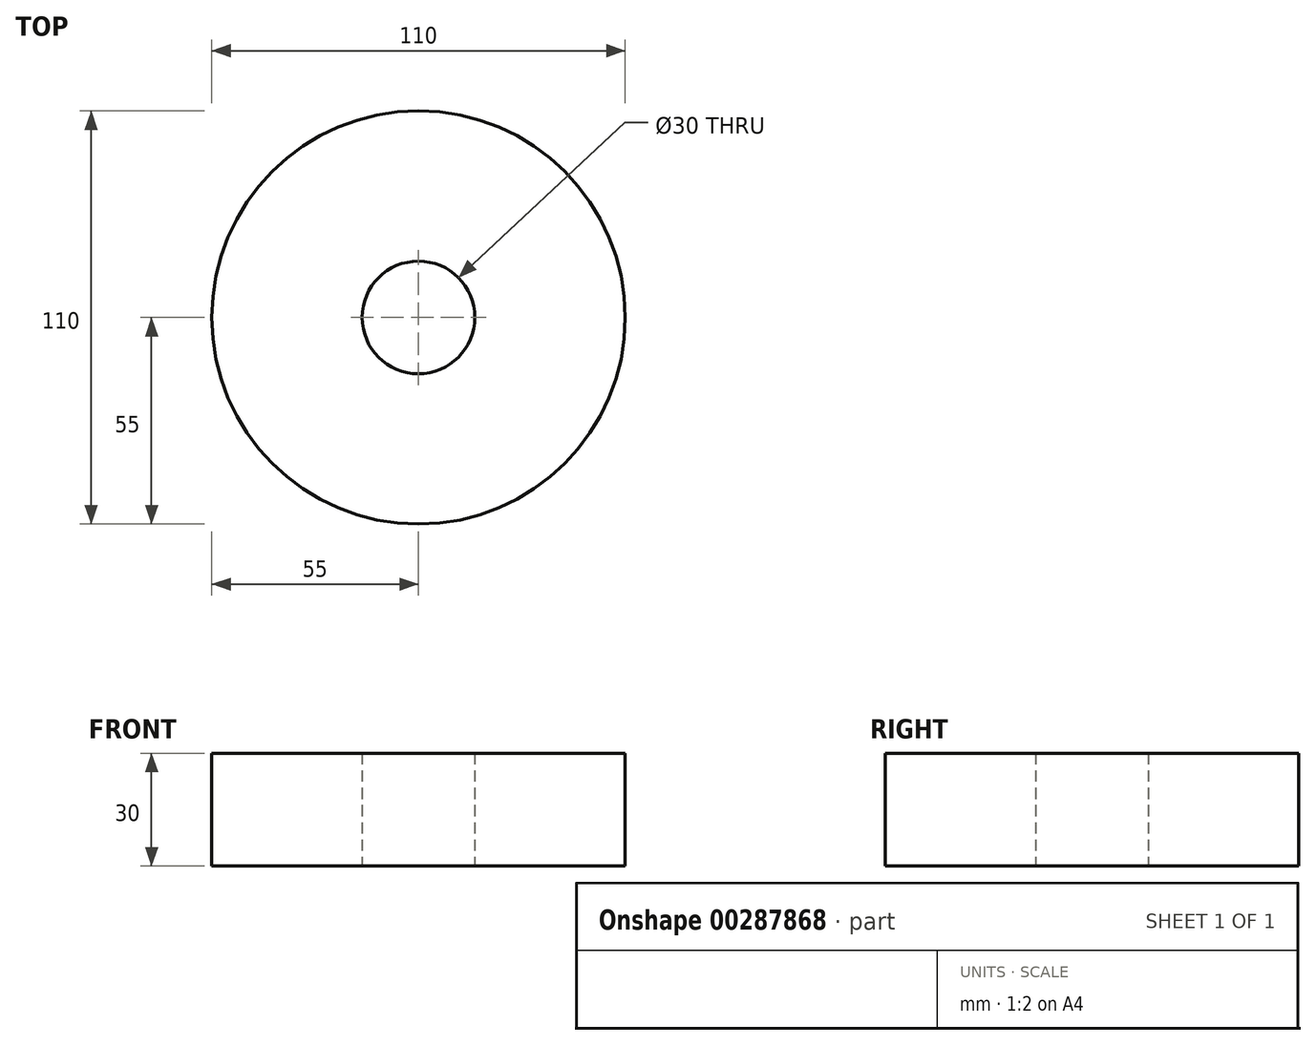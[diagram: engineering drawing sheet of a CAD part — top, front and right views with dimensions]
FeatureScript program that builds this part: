
annotation { "Feature Type Name" : "Feature", "Feature Type Description" : "" }
export const myFeature = defineFeature(function(context is Context, id is Id, definition is map)
    precondition{}
    {
        {
            var Q0;
            Q0=qCreatedBy(makeId("Top.planeOp"),FACE);
            var sketch = newSketch(context, id + "F0", { "sketchPlane" : qUnion([Q0])});
            skCircle(sketch, "E0", {"center": v(0, 0) * mm, "radius": 55 * mm});
            skCircle(sketch, "E1", {"center": v(0, 0) * mm, "radius": 15 * mm});
            skSolve(sketch);
        }
        {
            var Q0;
            Q0 = qSketchRegion(id + "F0", true);
            extrude(context, id + "F1", {"entities" : qUnion([Q0]), "depth" : 30 * mm});
        }
    });
